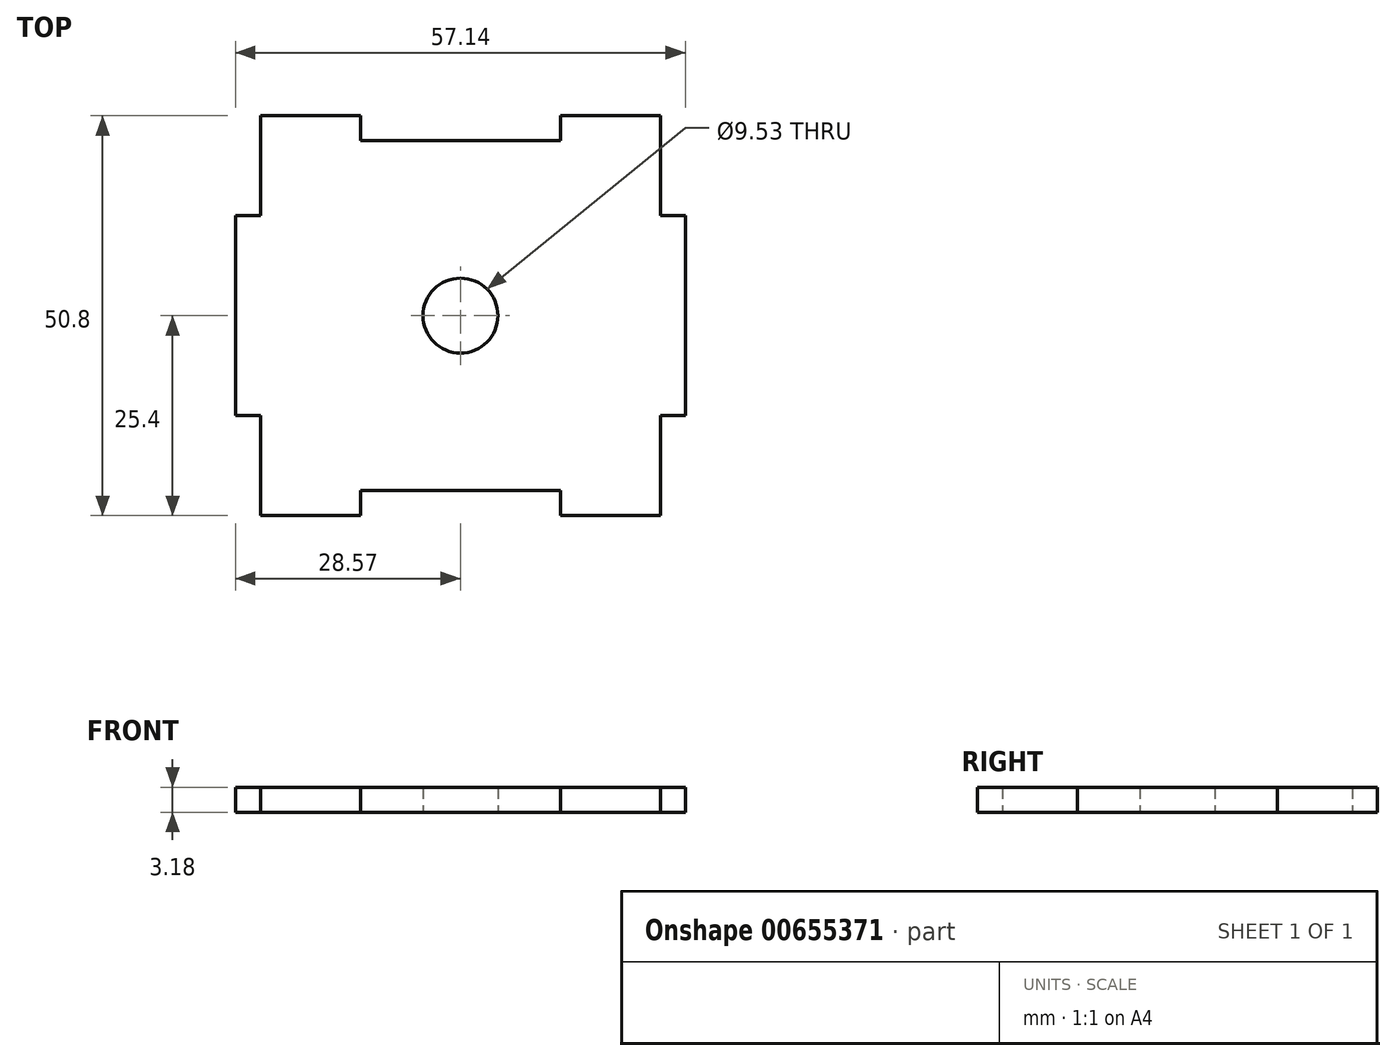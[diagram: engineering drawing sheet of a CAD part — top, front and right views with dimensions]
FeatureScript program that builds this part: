
annotation { "Feature Type Name" : "Feature", "Feature Type Description" : "" }
export const myFeature = defineFeature(function(context is Context, id is Id, definition is map)
    precondition{}
    {
        {
            var Q0;
            Q0=qCreatedBy(makeId("Top.planeOp"),FACE);
            var sketch = newSketch(context, id + "F0", { "sketchPlane" : qUnion([Q0])});
            skLineSegment(sketch, "E0.bottom", {"start": v(25.4, 25.4) * mm, "end": v(-25.4, 25.4) * mm});
            skLineSegment(sketch, "E0.top", {"start": v(25.4, -25.4) * mm, "end": v(-25.4, -25.4) * mm});
            skLineSegment(sketch, "E0.left", {"start": v(25.4, 25.4) * mm, "end": v(25.4, -25.4) * mm});
            skLineSegment(sketch, "E0.right", {"start": v(-25.4, 25.4) * mm, "end": v(-25.4, -25.4) * mm});
            skPoint(sketch, "E0.middle", {"position": v(0, 0) * mm});
            skLineSegment(sketch, "E1.bottom", {"start": v(12.7, 22.22) * mm, "end": v(-12.7, 22.22) * mm});
            skLineSegment(sketch, "E1.top", {"start": v(12.7, 28.58) * mm, "end": v(-12.7, 28.58) * mm});
            skLineSegment(sketch, "E1.left", {"start": v(12.7, 22.23) * mm, "end": v(12.7, 28.58) * mm});
            skLineSegment(sketch, "E1.right", {"start": v(-12.7, 22.22) * mm, "end": v(-12.7, 28.57) * mm});
            skPoint(sketch, "E1.middle", {"position": v(0, 25.4) * mm});
            skLineSegment(sketch, "E2.bottom", {"start": v(28.57, 12.7) * mm, "end": v(22.22, 12.7) * mm});
            skLineSegment(sketch, "E2.top", {"start": v(28.57, -12.7) * mm, "end": v(22.22, -12.7) * mm});
            skLineSegment(sketch, "E2.left", {"start": v(28.57, 12.7) * mm, "end": v(28.57, -12.7) * mm});
            skLineSegment(sketch, "E2.right", {"start": v(22.22, 12.7) * mm, "end": v(22.22, -12.7) * mm});
            skPoint(sketch, "E2.middle", {"position": v(25.4, 0) * mm});
            skLineSegment(sketch, "E3.bottom", {"start": v(-22.22, 12.7) * mm, "end": v(-28.57, 12.7) * mm});
            skLineSegment(sketch, "E3.top", {"start": v(-22.22, -12.7) * mm, "end": v(-28.57, -12.7) * mm});
            skLineSegment(sketch, "E3.left", {"start": v(-22.22, 12.7) * mm, "end": v(-22.22, -12.7) * mm});
            skLineSegment(sketch, "E3.right", {"start": v(-28.57, 12.7) * mm, "end": v(-28.57, -12.7) * mm});
            skPoint(sketch, "E3.middle", {"position": v(-25.4, 0) * mm});
            skLineSegment(sketch, "E4.bottom", {"start": v(12.7, -22.23) * mm, "end": v(-12.7, -22.23) * mm});
            skLineSegment(sketch, "E4.top", {"start": v(12.7, -28.58) * mm, "end": v(-12.7, -28.58) * mm});
            skLineSegment(sketch, "E4.left", {"start": v(12.7, -22.23) * mm, "end": v(12.7, -28.58) * mm});
            skLineSegment(sketch, "E4.right", {"start": v(-12.7, -22.23) * mm, "end": v(-12.7, -28.58) * mm});
            skPoint(sketch, "E4.middle", {"position": v(0, -25.4) * mm});
            skCircle(sketch, "E5", {"center": v(0, 0) * mm, "radius": 4.76 * mm});
            skSolve(sketch);
        }
        {
            var Q0;
            {var subQ0=sQuery(id+"F0.wireOp",EDGE,"E1.bottom");Q0=makeQuery(id+"F0.imprint","IMPRINT",FACE,{"disambiguationData":[TD([[makeQuery(id+"F0.imprint","IMPRINT",EDGE,{"derivedFrom":subQ0}),1.0]])]});}
            var Q1;
            {var subQ5=sQuery(id+"F0.wireOp",EDGE,"E3.right");Q1=makeQuery(id+"F0.imprint","IMPRINT",FACE,{"disambiguationData":[TD([[makeQuery(id+"F0.imprint","IMPRINT",EDGE,{"derivedFrom":subQ5}),1.0]])]});}
            var Q2;
            {var subQ5=sQuery(id+"F0.wireOp",EDGE,"E3.left");Q2=makeQuery(id+"F0.imprint","IMPRINT",FACE,{"disambiguationData":[TD([[makeQuery(id+"F0.imprint","IMPRINT",EDGE,{"derivedFrom":subQ5}),-1.0]])]});}
            var Q3;
            {var subQ5=sQuery(id+"F0.wireOp",EDGE,"E2.left");Q3=makeQuery(id+"F0.imprint","IMPRINT",FACE,{"disambiguationData":[TD([[makeQuery(id+"F0.imprint","IMPRINT",EDGE,{"derivedFrom":subQ5}),-1.0]])]});}
            var Q4;
            {var subQ5=sQuery(id+"F0.wireOp",EDGE,"E2.right");Q4=makeQuery(id+"F0.imprint","IMPRINT",FACE,{"disambiguationData":[TD([[makeQuery(id+"F0.imprint","IMPRINT",EDGE,{"derivedFrom":subQ5}),1.0]])]});}
            extrude(context, id + "F1", {"entities" : qUnion([Q0, Q1, Q2, Q3, Q4]), "depth" : 3.17 * mm, "offsetDistance" : 25.4 * mm});
        }
    });
